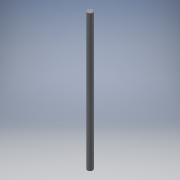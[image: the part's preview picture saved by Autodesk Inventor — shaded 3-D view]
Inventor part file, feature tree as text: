
AUTODESK INVENTOR PART (.ipt)
format: ipt  version: 2017 (Build 210142000, 142)  size: 88,064 bytes
history: native  units: mm
features: extrude x1, sketch x1
ambient origin geometry x8: Origin, YZ Plane, XZ Plane, XY Plane, X Axis, Y Axis, Z Axis, Center Point
bodies: Solid1 (feature_tree)
feature tree (2):
  extrude  "Extrusion1"  Depth=500.0mm TaperAngle=0.0deg
  sketch  "Sketch1"  dims[d0=20.0mm d1=500.0mm d2=0.0mm]
